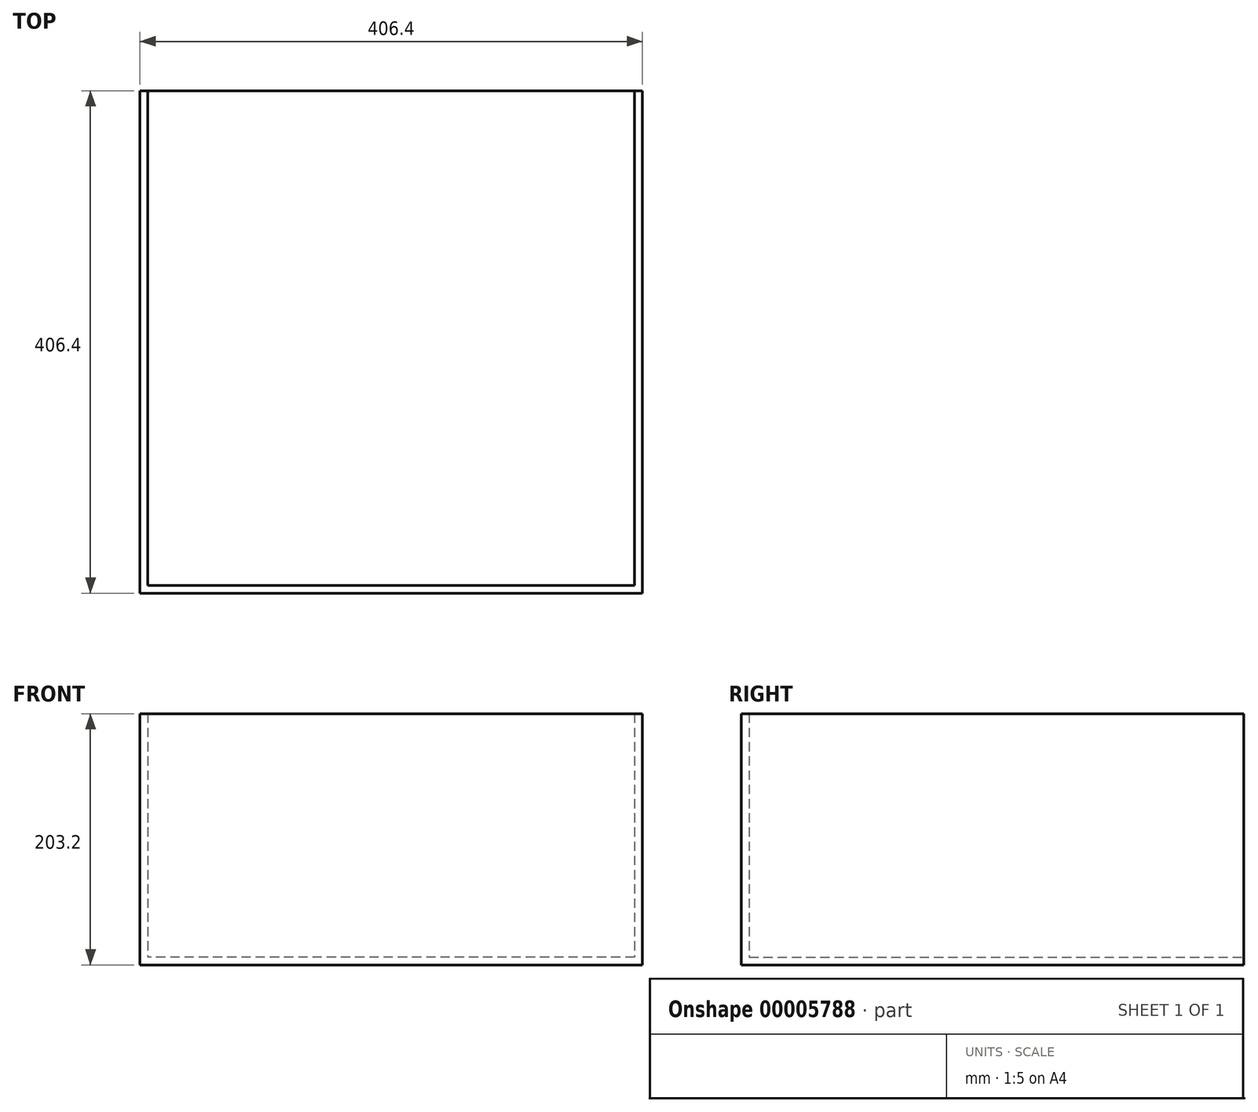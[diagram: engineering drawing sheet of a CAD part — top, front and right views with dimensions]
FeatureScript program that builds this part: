
annotation { "Feature Type Name" : "Feature", "Feature Type Description" : "" }
export const myFeature = defineFeature(function(context is Context, id is Id, definition is map)
    precondition{}
    {
        {
            var Q0;
            Q0=qCreatedBy(makeId("Top.planeOp"),FACE);
            var sketch = newSketch(context, id + "F0", { "sketchPlane" : qUnion([Q0])});
            skLineSegment(sketch, "E0.rect.bottom", {"start": v(203.2, -203.2) * mm, "end": v(-203.2, -203.2) * mm});
            skLineSegment(sketch, "E0.rect.top", {"start": v(203.2, 203.2) * mm, "end": v(-203.2, 203.2) * mm});
            skLineSegment(sketch, "E0.rect.left", {"start": v(203.2, -203.2) * mm, "end": v(203.2, 203.2) * mm});
            skLineSegment(sketch, "E0.rect.right", {"start": v(-203.2, -203.2) * mm, "end": v(-203.2, 203.2) * mm});
            skPoint(sketch, "E0.rect.middle", {"position": v(0, 0) * mm});
            skSolve(sketch);
        }
        {
            var Q0;
            Q0=makeQuery(id+"F0.imprint","IMPRINT",FACE,{"disambiguationData":[TD([[makeQuery(id+"F0.imprint","IMPRINT",EDGE,{"derivedFrom":sQuery(id+"F0.wireOp",EDGE,"E0.rect.bottom")}),-1.0]])]});
            extrude(context, id + "F1", {"entities" : qUnion([Q0]), "depth" : 203.2 * mm});
        }
        {
            var Q0;
            Q0=makeQuery(id+"F1.opExtrude","CAP_FACE",FACE,{"disambiguationData":[OSD([sQuery(id+"F0.wireOp",EDGE,"E0.rect.bottom"),sQuery(id+"F0.wireOp",EDGE,"E0.rect.top"),sQuery(id+"F0.wireOp",EDGE,"E0.rect.left"),sQuery(id+"F0.wireOp",EDGE,"E0.rect.right")])],"isStart":false});
            var Q1;
            Q1=makeQuery(id+"F1.opExtrude","SWEPT_FACE",FACE,{"disambiguationData":[OSD([sQuery(id+"F0.wireOp",EDGE,"E0.rect.top")])]});
            shell(context, id + "F2", {"entities" : qUnion([Q0, Q1]), "thickness" : 6.35 * mm});
        }
    });
